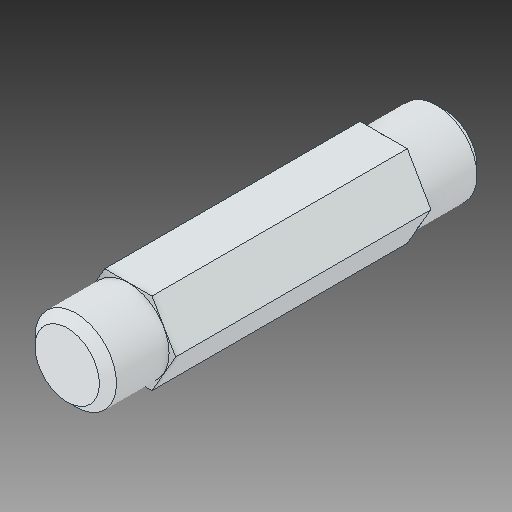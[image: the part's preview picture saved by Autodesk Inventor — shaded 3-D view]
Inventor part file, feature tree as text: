
AUTODESK INVENTOR PART (.ipt)
format: ipt  version: 2017 (Build 210142000, 142)  size: 102,400 bytes
history: native  units: in
note: dims shown in document units (in); Inventor stores cm internally (conversion verified against a paired STEP export)
features: chamfer x1
ambient origin geometry x8: Origin, YZ Plane, XZ Plane, XY Plane, X Axis, Y Axis, Z Axis, Center Point
bodies: Solid1 (feature_tree)
feature tree (1):
  chamfer  "Chamfer1"  [1 undecoded]
note: 1 required parameter value undecoded (feature->parameter linkage not recoverable at this tier; creation-order binding heuristic only, values carry confidence <= 0.55)
